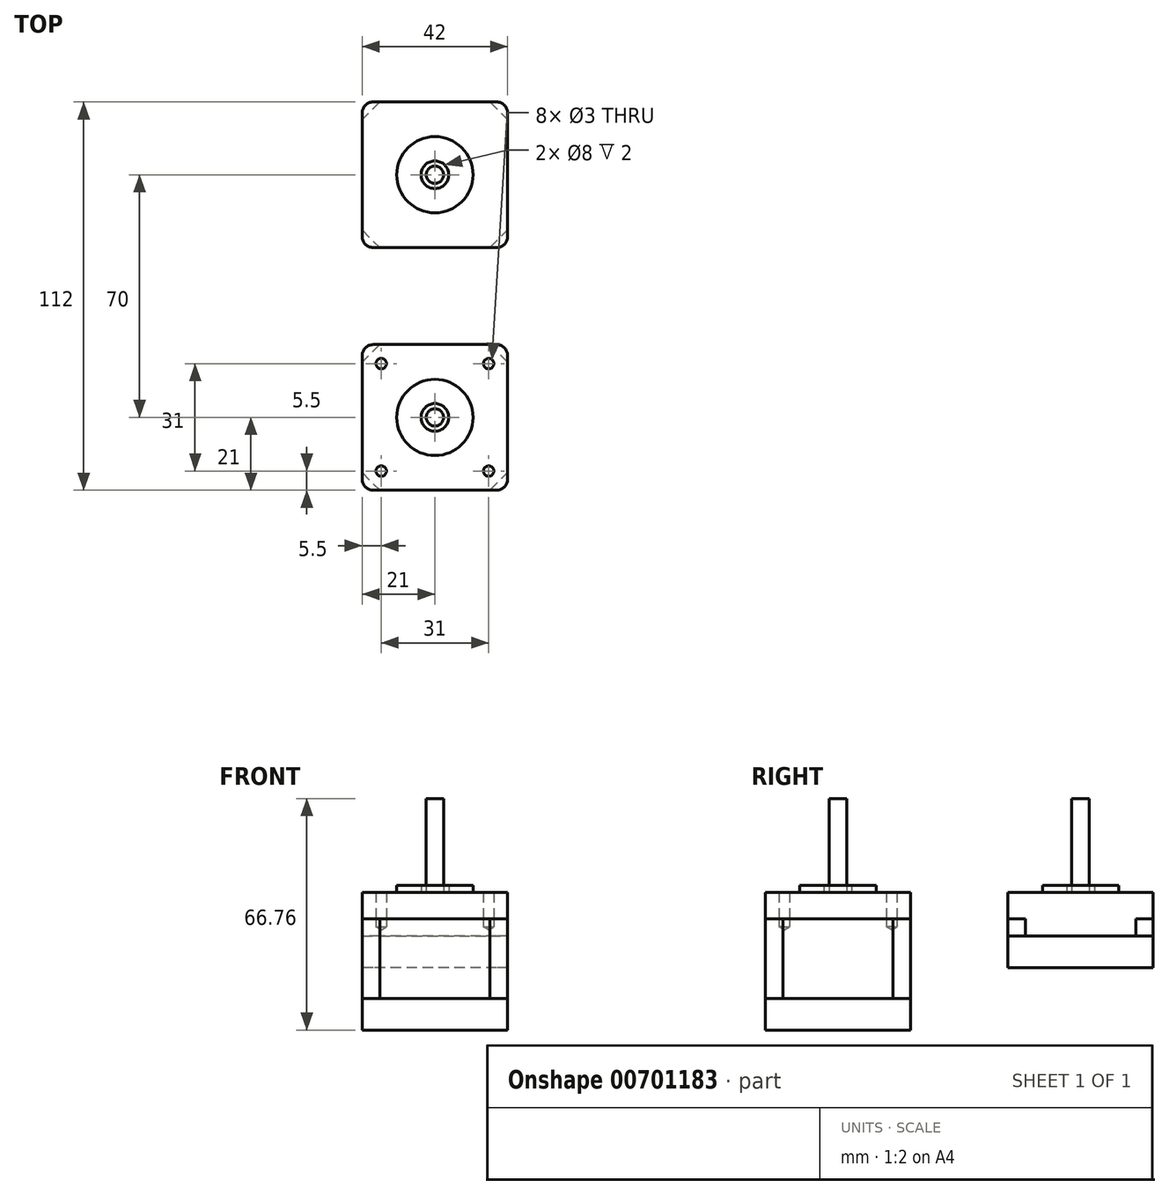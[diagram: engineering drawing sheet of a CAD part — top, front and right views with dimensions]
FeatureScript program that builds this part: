
annotation { "Feature Type Name" : "Feature", "Feature Type Description" : "" }
export const myFeature = defineFeature(function(context is Context, id is Id, definition is map)
    precondition{}
    {
        {
            var Q0;
            Q0=qCreatedBy(makeId("Top.planeOp"),FACE);
            var sketch = newSketch(context, id + "F0", { "sketchPlane" : qUnion([Q0])});
            skLineSegment(sketch, "E0.bottom", {"start": v(21, -21) * mm, "end": v(-21, -21) * mm});
            skLineSegment(sketch, "E0.top", {"start": v(21, 21) * mm, "end": v(-21, 21) * mm});
            skLineSegment(sketch, "E0.left", {"start": v(21, -21) * mm, "end": v(21, 21) * mm});
            skLineSegment(sketch, "E0.right", {"start": v(-21, -21) * mm, "end": v(-21, 21) * mm});
            skPoint(sketch, "E0.middle", {"position": v(0, 0) * mm});
            skLineSegment(sketch, "E1.bottom", {"start": v(21, 49) * mm, "end": v(-21, 49) * mm});
            skLineSegment(sketch, "E1.top", {"start": v(21, 91) * mm, "end": v(-21, 91) * mm});
            skLineSegment(sketch, "E1.left", {"start": v(21, 49) * mm, "end": v(21, 91) * mm});
            skLineSegment(sketch, "E1.right", {"start": v(-21, 49) * mm, "end": v(-21, 91) * mm});
            skPoint(sketch, "E1.middle", {"position": v(0, 70) * mm});
            skSolve(sketch);
        }
        {
            var Q0;
            Q0=makeQuery(id+"F0.imprint","IMPRINT",FACE,{"disambiguationData":[TD([[makeQuery(id+"F0.imprint","IMPRINT",EDGE,{"derivedFrom":sQuery(id+"F0.wireOp",EDGE,"E0.bottom")}),-1.0]])]});
            var Q1;
            Q1=makeQuery(id+"F0.imprint","IMPRINT",FACE,{"disambiguationData":[TD([[makeQuery(id+"F0.imprint","IMPRINT",EDGE,{"derivedFrom":sQuery(id+"F0.wireOp",EDGE,"E1.bottom")}),-1.0]])]});
            extrude(context, id + "F1", {"entities" : qUnion([Q0, Q1]), "depth" : 7.66 * mm, "offsetDistance" : 25 * mm});
        }
        {
            var Q0;
            Q0=makeQuery(id+"F1.opExtrude","CAP_FACE",FACE,{"disambiguationData":[OSD([sQuery(id+"F0.wireOp",EDGE,"E0.bottom"),sQuery(id+"F0.wireOp",EDGE,"E0.top"),sQuery(id+"F0.wireOp",EDGE,"E0.left"),sQuery(id+"F0.wireOp",EDGE,"E0.right")])],"isStart":false});
            var sketch = newSketch(context, id + "F2", { "sketchPlane" : qUnion([Q0])});
            skCircle(sketch, "E2", {"center": v(0, 0) * mm, "radius": 11 * mm});
            skCircle(sketch, "E3", {"center": v(15.5, 15.5) * mm, "radius": 1.5 * mm});
            skCircle(sketch, "E4", {"center": v(-15.5, 15.5) * mm, "radius": 1.5 * mm});
            skCircle(sketch, "E5", {"center": v(-15.5, -15.5) * mm, "radius": 1.5 * mm});
            skCircle(sketch, "E6", {"center": v(15.5, -15.5) * mm, "radius": 1.5 * mm});
            skCircle(sketch, "E7", {"center": v(0, 0) * mm, "radius": 2.5 * mm});
            skCircle(sketch, "E8", {"center": v(0, 0) * mm, "radius": 4 * mm});
            skCircle(sketch, "E9", {"center": v(15.5, 54.5) * mm, "radius": 1.5 * mm});
            skPoint(sketch, "E10", {"position": v(0, 70) * mm});
            skCircle(sketch, "E11", {"center": v(0, 70) * mm, "radius": 2.5 * mm});
            skCircle(sketch, "E12", {"center": v(0, 70) * mm, "radius": 4 * mm});
            skCircle(sketch, "E13", {"center": v(0, 70) * mm, "radius": 11 * mm});
            skCircle(sketch, "E14", {"center": v(15.5, 85.5) * mm, "radius": 1.5 * mm});
            skCircle(sketch, "E15", {"center": v(-15.5, 85.5) * mm, "radius": 1.5 * mm});
            skCircle(sketch, "E16", {"center": v(-15.5, 54.5) * mm, "radius": 1.5 * mm});
            skSolve(sketch);
        }
        {
            var Q0;
            Q0=makeQuery(id+"F2.imprint","IMPRINT",FACE,{"disambiguationData":[TD([[makeQuery(id+"F2.imprint","IMPRINT",EDGE,{"derivedFrom":sQuery(id+"F2.wireOp",EDGE,"E2")}),1.0]])]});
            var Q1;
            Q1=makeQuery(id+"F2.imprint","IMPRINT",FACE,{"disambiguationData":[TD([[makeQuery(id+"F2.imprint","IMPRINT",EDGE,{"derivedFrom":sQuery(id+"F2.wireOp",EDGE,"E12")}),-1.0]])]});
            extrude(context, id + "F3", {"entities" : qUnion([Q0, Q1]), "operationType" : NewBodyOperationType.ADD, "depth" : 2 * mm, "offsetDistance" : 25 * mm});
        }
        {
            var Q0;
            Q0=makeQuery(id+"F1.opExtrude","CAP_FACE",FACE,{"disambiguationData":[OSD([sQuery(id+"F0.wireOp",EDGE,"E0.bottom"),sQuery(id+"F0.wireOp",EDGE,"E0.top"),sQuery(id+"F0.wireOp",EDGE,"E0.left"),sQuery(id+"F0.wireOp",EDGE,"E0.right")])],"isStart":true});
            var sketch = newSketch(context, id + "F4", { "sketchPlane" : qUnion([Q0])});
            skLineSegment(sketch, "E17", {"start": v(-15.92, -21) * mm, "end": v(-21, -15.92) * mm});
            skLineSegment(sketch, "E18", {"start": v(-21, -15.92) * mm, "end": v(-21, 15.92) * mm});
            skLineSegment(sketch, "E19", {"start": v(-21, 15.92) * mm, "end": v(-15.92, 21) * mm});
            skLineSegment(sketch, "E20", {"start": v(-15.92, 21) * mm, "end": v(15.92, 21) * mm});
            skLineSegment(sketch, "E21", {"start": v(15.92, 21) * mm, "end": v(21, 15.92) * mm});
            skLineSegment(sketch, "E22", {"start": v(21, 15.92) * mm, "end": v(21, -15.92) * mm});
            skLineSegment(sketch, "E23", {"start": v(21, -15.92) * mm, "end": v(15.92, -21) * mm});
            skLineSegment(sketch, "E24", {"start": v(15.92, -21) * mm, "end": v(-15.92, -21) * mm});
            skLineSegment(sketch, "E25", {"start": v(-15.92, -91) * mm, "end": v(-21, -85.92) * mm});
            skLineSegment(sketch, "E26", {"start": v(-21, -85.92) * mm, "end": v(-21, -54.08) * mm});
            skLineSegment(sketch, "E27", {"start": v(-21, -54.08) * mm, "end": v(-15.92, -49) * mm});
            skLineSegment(sketch, "E28", {"start": v(-15.92, -49) * mm, "end": v(15.92, -49) * mm});
            skLineSegment(sketch, "E29", {"start": v(15.92, -49) * mm, "end": v(21, -54.08) * mm});
            skLineSegment(sketch, "E30", {"start": v(21, -54.08) * mm, "end": v(21, -85.92) * mm});
            skLineSegment(sketch, "E31", {"start": v(-15.92, -91) * mm, "end": v(15.92, -91) * mm});
            skLineSegment(sketch, "E32", {"start": v(15.92, -91) * mm, "end": v(21, -85.92) * mm});
            skSolve(sketch);
        }
        {
            var Q0;
            Q0=makeQuery(id+"F4.imprint","IMPRINT",FACE,{"disambiguationData":[TD([[makeQuery(id+"F4.imprint","IMPRINT",EDGE,{"derivedFrom":sQuery(id+"F4.wireOp",EDGE,"E17")}),-1.0]])]});
            extrude(context, id + "F5", {"entities" : qUnion([Q0]), "depth" : 23 * mm, "offsetDistance" : 25 * mm});
        }
        {
            var Q0;
            Q0=makeQuery(id+"F4.imprint","IMPRINT",FACE,{"disambiguationData":[TD([[makeQuery(id+"F4.imprint","IMPRINT",EDGE,{"derivedFrom":sQuery(id+"F4.wireOp",EDGE,"E25")}),-1.0]])]});
            var Q1;
            Q1=sQuery(id+"F4.wireOp",EDGE,"E28");
            var Q2;
            Q2=sQuery(id+"F4.wireOp",EDGE,"E27");
            var Q3;
            Q3=sQuery(id+"F4.wireOp",EDGE,"E26");
            extrude(context, id + "F6", {"entities" : qUnion([Q0]), "operationType" : NewBodyOperationType.ADD, "surfaceEntities" : qUnion([Q1, Q2, Q3]), "depth" : 5 * mm, "offsetDistance" : 25 * mm});
        }
        {
            var Q0;
            Q0=makeQuery(id+"F5.opExtrude","CAP_FACE",FACE,{"disambiguationData":[OSD([sQuery(id+"F4.wireOp",EDGE,"E17"),sQuery(id+"F4.wireOp",EDGE,"E18"),sQuery(id+"F4.wireOp",EDGE,"E19"),sQuery(id+"F4.wireOp",EDGE,"E20"),sQuery(id+"F4.wireOp",EDGE,"E21"),sQuery(id+"F4.wireOp",EDGE,"E22"),sQuery(id+"F4.wireOp",EDGE,"E23"),sQuery(id+"F4.wireOp",EDGE,"E24")])],"isStart":false});
            var sketch = newSketch(context, id + "F7", { "sketchPlane" : qUnion([Q0])});
            skLineSegment(sketch, "E33.bottom", {"start": v(21, -21) * mm, "end": v(-21, -21) * mm});
            skLineSegment(sketch, "E33.top", {"start": v(21, 21) * mm, "end": v(-21, 21) * mm});
            skLineSegment(sketch, "E33.left", {"start": v(21, -21) * mm, "end": v(21, 21) * mm});
            skLineSegment(sketch, "E33.right", {"start": v(-21, -21) * mm, "end": v(-21, 21) * mm});
            skPoint(sketch, "E33.middle", {"position": v(0, 0) * mm});
            skSolve(sketch);
        }
        {
            var Q0;
            Q0=makeQuery(id+"F6.opExtrude","CAP_FACE",FACE,{"disambiguationData":[OSD([sQuery(id+"F4.wireOp",EDGE,"E25"),sQuery(id+"F4.wireOp",EDGE,"E26"),sQuery(id+"F4.wireOp",EDGE,"E27"),sQuery(id+"F4.wireOp",EDGE,"E28"),sQuery(id+"F4.wireOp",EDGE,"E29"),sQuery(id+"F4.wireOp",EDGE,"E30"),sQuery(id+"F4.wireOp",EDGE,"E31"),sQuery(id+"F4.wireOp",EDGE,"E32")])],"isStart":false});
            var sketch = newSketch(context, id + "F8", { "sketchPlane" : qUnion([Q0])});
            skLineSegment(sketch, "E34.bottom", {"start": v(21, -91) * mm, "end": v(-21, -91) * mm});
            skLineSegment(sketch, "E34.top", {"start": v(21, -49) * mm, "end": v(-21, -49) * mm});
            skLineSegment(sketch, "E34.left", {"start": v(21, -91) * mm, "end": v(21, -49) * mm});
            skLineSegment(sketch, "E34.right", {"start": v(-21, -91) * mm, "end": v(-21, -49) * mm});
            skPoint(sketch, "E34.middle", {"position": v(0, -70) * mm});
            skSolve(sketch);
        }
        {
            var Q0;
            Q0 = qSketchRegion(id + "F7", true);
            var Q1;
            Q1 = qSketchRegion(id + "F8", true);
            extrude(context, id + "F9", {"entities" : qUnion([Q0, Q1]), "depth" : 9.1 * mm, "offsetDistance" : 25 * mm});
        }
        {
            var Q0;
            Q0=makeQuery(id+"F1.opExtrude","SWEPT_EDGE",EDGE,{"disambiguationData":[OSD([sQuery(id+"F0.wireOp",EDGE,"E0.top"),sQuery(id+"F0.wireOp",EDGE,"E0.left")])]});
            var Q1;
            Q1=makeQuery(id+"F1.opExtrude","SWEPT_EDGE",EDGE,{"disambiguationData":[OSD([sQuery(id+"F0.wireOp",EDGE,"E0.bottom"),sQuery(id+"F0.wireOp",EDGE,"E0.left")])]});
            var Q2;
            Q2=makeQuery(id+"F1.opExtrude","SWEPT_EDGE",EDGE,{"disambiguationData":[OSD([sQuery(id+"F0.wireOp",EDGE,"E0.bottom"),sQuery(id+"F0.wireOp",EDGE,"E0.right")])]});
            var Q3;
            Q3=makeQuery(id+"F1.opExtrude","SWEPT_EDGE",EDGE,{"disambiguationData":[OSD([sQuery(id+"F0.wireOp",EDGE,"E0.top"),sQuery(id+"F0.wireOp",EDGE,"E0.right")])]});
            var Q4;
            Q4=makeQuery(id+"F9.opExtrude","SWEPT_EDGE",EDGE,{"disambiguationData":[OSD([sQuery(id+"F7.wireOp",EDGE,"E33.top"),sQuery(id+"F7.wireOp",EDGE,"E33.left")])]});
            var Q5;
            Q5=makeQuery(id+"F9.opExtrude","SWEPT_EDGE",EDGE,{"disambiguationData":[OSD([sQuery(id+"F7.wireOp",EDGE,"E33.bottom"),sQuery(id+"F7.wireOp",EDGE,"E33.right")])]});
            var Q6;
            Q6=makeQuery(id+"F9.opExtrude","SWEPT_EDGE",EDGE,{"disambiguationData":[OSD([sQuery(id+"F7.wireOp",EDGE,"E33.top"),sQuery(id+"F7.wireOp",EDGE,"E33.right")])]});
            var Q7;
            Q7=makeQuery(id+"F9.opExtrude","SWEPT_EDGE",EDGE,{"disambiguationData":[OSD([sQuery(id+"F7.wireOp",EDGE,"E33.bottom"),sQuery(id+"F7.wireOp",EDGE,"E33.left")])]});
            var Q8;
            Q8=makeQuery(id+"F1.opExtrude","SWEPT_EDGE",EDGE,{"disambiguationData":[OSD([sQuery(id+"F0.wireOp",EDGE,"E1.top"),sQuery(id+"F0.wireOp",EDGE,"E1.right")])]});
            var Q9;
            Q9=makeQuery(id+"F9.opExtrude","SWEPT_EDGE",EDGE,{"disambiguationData":[OSD([sQuery(id+"F7.wireOp",EDGE,"XkL0GJ3n-95pS-ixZf-LIlK-itM533q9Re1m.bottom"),sQuery(id+"F7.wireOp",EDGE,"XkL0GJ3n-95pS-ixZf-LIlK-itM533q9Re1m.right")])]});
            var Q10;
            Q10=makeQuery(id+"F9.opExtrude","SWEPT_EDGE",EDGE,{"disambiguationData":[OSD([sQuery(id+"F7.wireOp",EDGE,"XkL0GJ3n-95pS-ixZf-LIlK-itM533q9Re1m.top"),sQuery(id+"F7.wireOp",EDGE,"XkL0GJ3n-95pS-ixZf-LIlK-itM533q9Re1m.right")])]});
            var Q11;
            Q11=makeQuery(id+"F1.opExtrude","SWEPT_EDGE",EDGE,{"disambiguationData":[OSD([sQuery(id+"F0.wireOp",EDGE,"E1.bottom"),sQuery(id+"F0.wireOp",EDGE,"E1.right")])]});
            var Q12;
            Q12=makeQuery(id+"F9.opExtrude","SWEPT_EDGE",EDGE,{"disambiguationData":[OSD([sQuery(id+"F7.wireOp",EDGE,"XkL0GJ3n-95pS-ixZf-LIlK-itM533q9Re1m.bottom"),sQuery(id+"F7.wireOp",EDGE,"XkL0GJ3n-95pS-ixZf-LIlK-itM533q9Re1m.left")])]});
            var Q13;
            Q13=makeQuery(id+"F1.opExtrude","SWEPT_EDGE",EDGE,{"disambiguationData":[OSD([sQuery(id+"F0.wireOp",EDGE,"E1.top"),sQuery(id+"F0.wireOp",EDGE,"E1.left")])]});
            var Q14;
            Q14=makeQuery(id+"F9.opExtrude","SWEPT_EDGE",EDGE,{"disambiguationData":[OSD([sQuery(id+"F7.wireOp",EDGE,"XkL0GJ3n-95pS-ixZf-LIlK-itM533q9Re1m.top"),sQuery(id+"F7.wireOp",EDGE,"XkL0GJ3n-95pS-ixZf-LIlK-itM533q9Re1m.left")])]});
            var Q15;
            Q15=makeQuery(id+"F1.opExtrude","SWEPT_EDGE",EDGE,{"disambiguationData":[OSD([sQuery(id+"F0.wireOp",EDGE,"E1.bottom"),sQuery(id+"F0.wireOp",EDGE,"E1.left")])]});
            var Q16;
            Q16=makeQuery(id+"F9.opExtrude","SWEPT_EDGE",EDGE,{"disambiguationData":[OSD([sQuery(id+"F8.wireOp",EDGE,"E34.top"),sQuery(id+"F8.wireOp",EDGE,"E34.right")])]});
            var Q17;
            Q17=makeQuery(id+"F9.opExtrude","SWEPT_EDGE",EDGE,{"disambiguationData":[OSD([sQuery(id+"F8.wireOp",EDGE,"E34.bottom"),sQuery(id+"F8.wireOp",EDGE,"E34.right")])]});
            var Q18;
            Q18=makeQuery(id+"F9.opExtrude","SWEPT_EDGE",EDGE,{"disambiguationData":[OSD([sQuery(id+"F8.wireOp",EDGE,"E34.bottom"),sQuery(id+"F8.wireOp",EDGE,"E34.left")])]});
            var Q19;
            Q19=makeQuery(id+"F9.opExtrude","SWEPT_EDGE",EDGE,{"disambiguationData":[OSD([sQuery(id+"F8.wireOp",EDGE,"E34.top"),sQuery(id+"F8.wireOp",EDGE,"E34.left")])]});
            fillet(context, id + "F10", {"entities" : qUnion([Q0, Q1, Q2, Q3, Q4, Q5, Q6, Q7, Q8, Q9, Q10, Q11, Q12, Q13, Q14, Q15, Q16, Q17, Q18, Q19]), "radius" : 3.17 * mm, "tangentPropagation" : true, "defaultsChanged" : false, "vertexSettings" : [], "allowEdgeOverflow" : false});
        }
        {
            var Q0;
            Q0=sQuery(id+"F2.wireOp",VERTEX,"E3.center");
            var Q1;
            Q1=sQuery(id+"F2.wireOp",VERTEX,"E4.center");
            var Q2;
            Q2=sQuery(id+"F2.wireOp",VERTEX,"E6.center");
            var Q3;
            Q3=sQuery(id+"F2.wireOp",VERTEX,"E5.center");
            var Q4;
            Q4=sQuery(id+"F2.wireOp",VERTEX,"E9.center");
            var Q5;
            Q5=sQuery(id+"F2.wireOp",VERTEX,"E16.center");
            var Q6;
            Q6=sQuery(id+"F2.wireOp",VERTEX,"E15.center");
            var Q7;
            Q7=sQuery(id+"F2.wireOp",VERTEX,"E14.center");
            var Q8;
            Q8=makeQuery(id+"F1.opExtrude","SWEPT_BODY",BODY,{"disambiguationData":[OSD([sQuery(id+"F0.wireOp",EDGE,"E0.bottom"),sQuery(id+"F0.wireOp",EDGE,"E0.top"),sQuery(id+"F0.wireOp",EDGE,"E0.left"),sQuery(id+"F0.wireOp",EDGE,"E0.right")])]});
            var Q9;
            Q9=makeQuery(id+"F5.opExtrude","SWEPT_BODY",BODY,{"disambiguationData":[OSD([sQuery(id+"F4.wireOp",EDGE,"E17"),sQuery(id+"F4.wireOp",EDGE,"E18"),sQuery(id+"F4.wireOp",EDGE,"E19"),sQuery(id+"F4.wireOp",EDGE,"E20"),sQuery(id+"F4.wireOp",EDGE,"E21"),sQuery(id+"F4.wireOp",EDGE,"E22"),sQuery(id+"F4.wireOp",EDGE,"E23"),sQuery(id+"F4.wireOp",EDGE,"E24")])]});
            hole(context, id + "F11", {"style" : HoleStyle.SIMPLE, "endStyle" : HoleEndStyle.BLIND, "holeDiameter" : 3 * mm, "majorDiameter" : 5 * mm, "holeDepth" : 10 * mm, "isTappedThrough" : true, "tappedDepth" : 12 * mm, "tapClearance" : 3, "locations" : qUnion([Q0, Q1, Q2, Q3, Q4, Q5, Q6, Q7]), "scope" : qUnion([Q8, Q9]), "startStyle" : HoleStartStyle.PART});
        }
        {
            var Q0;
            Q0=makeQuery(id+"F2.imprint","IMPRINT",FACE,{"disambiguationData":[TD([[makeQuery(id+"F2.imprint","IMPRINT",EDGE,{"derivedFrom":sQuery(id+"F2.wireOp",EDGE,"E7")}),1.0]])]});
            var Q1;
            Q1=makeQuery(id+"F2.imprint","IMPRINT",FACE,{"disambiguationData":[TD([[makeQuery(id+"F2.imprint","IMPRINT",EDGE,{"derivedFrom":sQuery(id+"F2.wireOp",EDGE,"E11")}),1.0]])]});
            extrude(context, id + "F12", {"entities" : qUnion([Q0, Q1]), "depth" : 27 * mm, "offsetDistance" : 25 * mm});
        }
    });
